SOLIDWORKS PART (.sldprt)
format: sldprt  version: not decoded by parser v0  size: 172,544 bytes
history: native  units: mm
features: sketch x6, plane x4, extrude x4, material x1, sweep x1, fillet x1 (+10 scaffold rows collapsed)
feature tree (27):
  scaffold x10  (default folders/planes/origin — collapsed)
  material  "Matériau <non spécifié>"
  plane  "Plan de face"
  plane  "Plan de dessus"
  plane  "Plan de droite"
  sketch  "Esquisse1"  dims[c1.D7=~1.23067mm c1.D1=19.8mm c1.D2=10.2mm c1.D3=9.5mm c1.D4=2.5mm c1.D5=5.1mm c1.D6=9.5mm c2.D7=10.0mm c2.D8=~42.731717mm c3.D8=45.0deg c3.D7=7.5mm c4.D8=1.0mm c4.D9=1.5mm c4.D10=1.0mm]
  extrude  "Extrusion1"  Depth=6.3mm
  sketch  "Esquisse2"  dims[c1.D5=~0.369999mm c1.D1=~25.211372mm c2.D1=90.0deg c3.D1=3.15mm c3.D2=1.6mm c3.D3=8.8mm c3.D4=7.3mm]
  extrude  "Extrusion2"  Depth=4mm
  plane  "Plan1"  Offset=3.15mm
  sketch  "Esquisse7"  dims[D1=3.15mm D2=2.0mm D3=3.0mm D4=0.4mm D5=0.2mm D6=4.0mm]
  sketch  "Esquisse8"  dims[c1.D4=0.5mm c1.D1=5.0mm c1.D2=15.8mm c1.D3=1.5mm c2.D4=~21.289947mm c3.D4=90.0deg c3.D3=1.5mm]
  sweep  "Balayage1"
  sketch  "Esquisse9"  dims[D1=3.0mm D2=0.4mm D3=2.0mm D4=~3.581561mm]
  extrude  "Extrusion3"  Depth=5mm
  fillet  "Congé1"  Radius=1.499mm
  sketch  "Esquisse10"  dims[D1=~2.264715mm]
  extrude  "Extrusion4"  Depth=3.2mm
decode coverage: 11 of 12 modeling features carry decoded parameters
note: ~ marks probable driven/reference dimensions
note: suppression state not decoded; provenance and decode notes live in map.json
